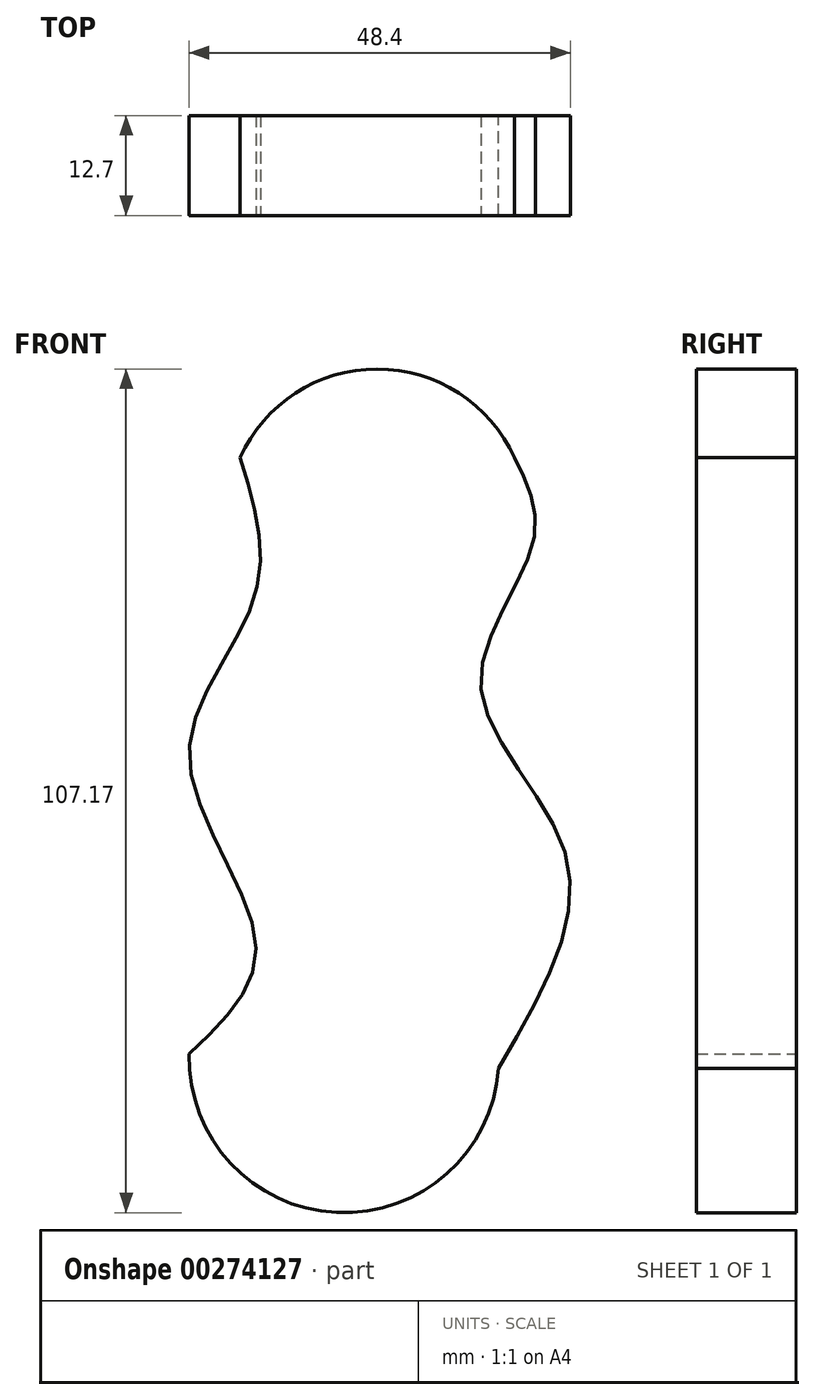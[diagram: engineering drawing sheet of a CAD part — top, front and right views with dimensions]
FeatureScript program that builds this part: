
annotation { "Feature Type Name" : "Feature", "Feature Type Description" : "" }
export const myFeature = defineFeature(function(context is Context, id is Id, definition is map)
    precondition{}
    {
        {
            var Q0;
            Q0=qCreatedBy(makeId("Front.planeOp"),FACE);
            var sketch = newSketch(context, id + "F0", { "sketchPlane" : qUnion([Q0])});
            skArc(sketch, "E0", {"start": v(-17.15, -21.75) * mm, "mid": v(1.59, -41.88) * mm, "end": v(22.12, -23.6) * mm});
            skFitSpline(sketch, "E1", {"points": [v(-17.15, -21.75) * mm, v(-8.66, -7.74) * mm, v(-17.15, 16.04) * mm, v(-8.85, 36.32) * mm, v(-10.7, 54.02) * mm], "startDerivative": vector(58.93, 56.26) * mm, "endDerivative": vector(-23.3, 75.67) * mm});
            skArc(sketch, "E2", {"start": v(24.15, 54.02) * mm, "mid": v(6.73, 65.27) * mm, "end": v(-10.7, 54.02) * mm});
            skFitSpline(sketch, "E3", {"points": [v(24.15, 54.02) * mm, v(26.55, 43.32) * mm, v(19.91, 24.89) * mm, v(30.79, 3.13) * mm, v(22.12, -23.6) * mm], "startDerivative": vector(27.07, -54.27) * mm, "endDerivative": vector(-54.68, -93.8) * mm});
            skSolve(sketch);
        }
        {
            var Q0;
            Q0=makeQuery(id+"F0.imprint","IMPRINT",FACE,{"disambiguationData":[TD([[makeQuery(id+"F0.imprint","IMPRINT",EDGE,{"derivedFrom":sQuery(id+"F0.wireOp",EDGE,"E0")}),1.0]])]});
            extrude(context, id + "F1", {"entities" : qUnion([Q0]), "depth" : 12.7 * mm});
        }
    });
